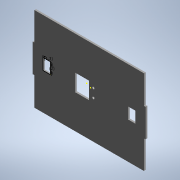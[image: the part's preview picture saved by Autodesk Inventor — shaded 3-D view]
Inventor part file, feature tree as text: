
AUTODESK INVENTOR PART (.ipt)
format: ipt  version: 2020 (Build 240168000, 168)  size: 193,536 bytes
history: native  units: mm (DEFAULTED — no unit token found)
features: sketch x20, extrude x13
ambient origin geometry x8: Origin, YZ Plane, XZ Plane, XY Plane, X Axis, Y Axis, Z Axis, Center Point
bodies: Solid1 (feature_tree)
feature tree (33):
  extrude  "Extrusion1"  Depth=3.0mm TaperAngle=0.0deg
  sketch  "Sketch2"  dims[d17=3.0mm d18=50.0mm]
  sketch  "Sketch3"  dims[d19=3.0mm d20=0.0mm d21=50.0mm]
  extrude  "Extrusion2"  Depth=50.0mm
  extrude  "Extrusion3"  Depth=50.0mm
  extrude  "Extrusion4"  Depth=3.0mm TaperAngle=0.0deg
  extrude  "Extrusion5"  Depth=3.0mm
  extrude  "Extrusion6"  Depth=15.0mm
  sketch  "Sketch9"  dims[d75=30.0mm d76=0.0mm d77=3.0mm d78=0.0mm]
  extrude  "Extrusion7"  Depth=3.0mm TaperAngle=0.0deg
  extrude  "Extrusion8"  Depth=30.0mm TaperAngle=0.0deg
  sketch  "Sketch12"  dims[d103=20.0mm d64=5.0mm]
  sketch  "Sketch13"  dims[d65=0.872665mm]
  extrude  "Extrusion9"  Depth=3.0mm TaperAngle=0.0deg
  extrude  "Extrusion10"  Depth=3.0mm TaperAngle=0.0deg
  extrude  "Extrusion11"  Depth=13.0mm
  extrude  "Extrusion12"  Depth=5.0mm
  extrude  "Extrusion13"  [1 undecoded]
  sketch  "Sketch19"
  sketch  "Sketch20"
  sketch  "Sketch1"  dims[d2=3.0mm d3=0.0mm d15=3.0mm d16=0.0mm]
  sketch  "Sketch4"  dims[d22=3.0mm d23=3.0mm d24=0.0mm]
  sketch  "Sketch5"  dims[d25=50.0mm d26=3.0mm]
  sketch  "Sketch6"  dims[d27=3.0mm d28=0.0mm d32=15.0mm]
  sketch  "Sketch7"  dims[d33=30.0mm d34=3.0mm d35=0.0mm]
  sketch  "Sketch8"  dims[d36=30.0mm d37=0.0mm d62=21.5mm d63=0.0mm]
  sketch  "Sketch10"  dims[d86=3.0mm d87=0.0mm d90=3.0mm d91=0.0mm]
  sketch  "Sketch11"  dims[d100=3.0mm d101=0.0mm d102=13.0mm]
  sketch  "Sketch14"
  sketch  "Sketch15"
  sketch  "Sketch16"
  sketch  "Sketch17"
  sketch  "Sketch18"
note: 1 required parameter value undecoded (feature->parameter linkage not recoverable at this tier; creation-order binding heuristic only, values carry confidence <= 0.55)
